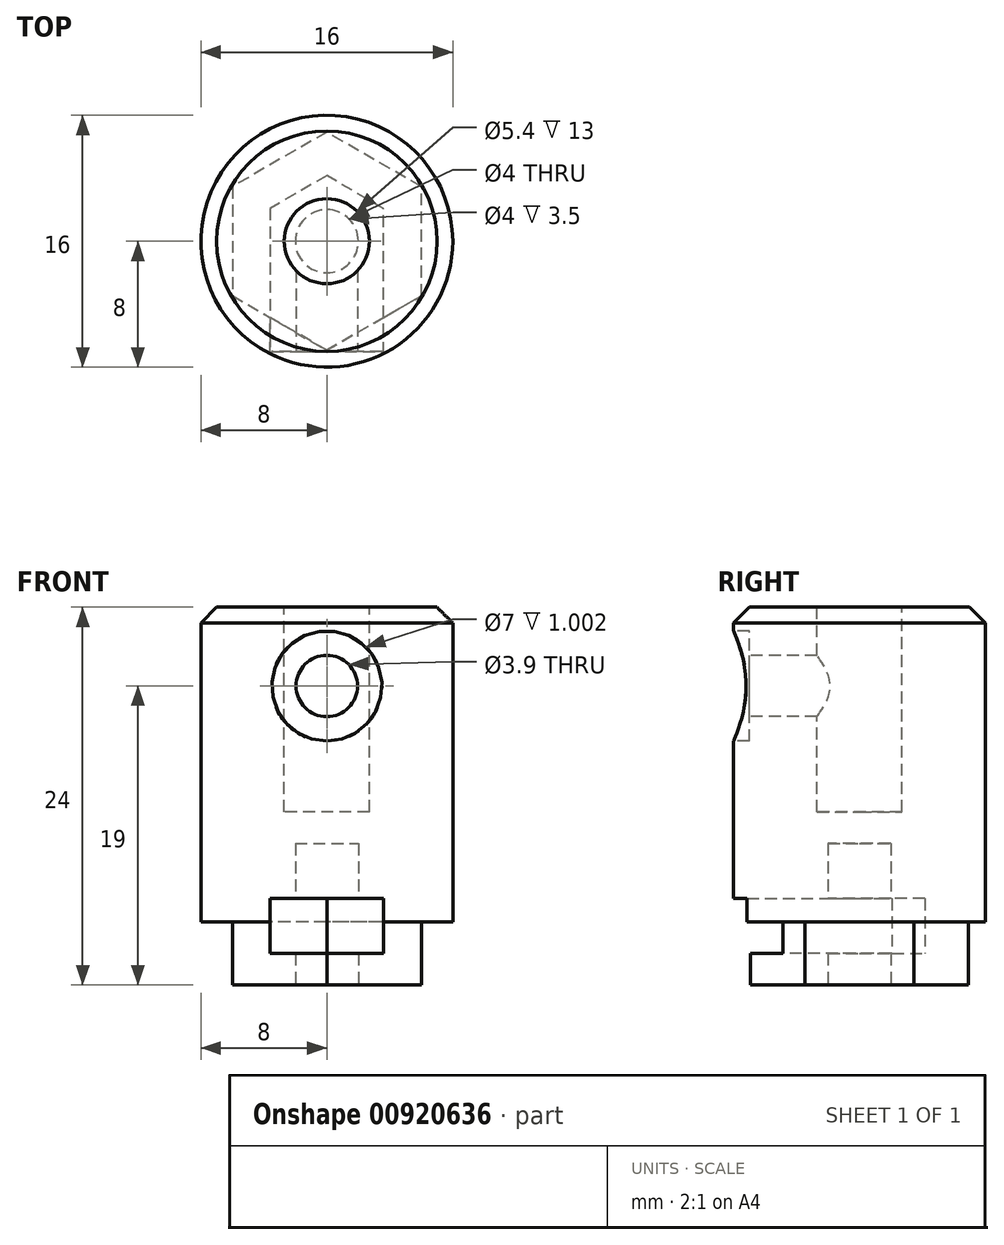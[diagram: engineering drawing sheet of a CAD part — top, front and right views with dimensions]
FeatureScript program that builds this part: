
annotation { "Feature Type Name" : "Feature", "Feature Type Description" : "" }
export const myFeature = defineFeature(function(context is Context, id is Id, definition is map)
    precondition{}
    {
        {
            assignVariable(context, id + "F0", {"name" : "len", "anyValue" : 20 * mm});
        }
        {
            var Q0;
            Q0=qCreatedBy(makeId("Top.planeOp"),FACE);
            var sketch = newSketch(context, id + "F1", { "sketchPlane" : qUnion([Q0])});
            skCircle(sketch, "E0", {"center": v(0, 0) * mm, "radius": 8 * mm});
            skSolve(sketch);
        }
        {
            var Q0;
            Q0=makeQuery(id+"F1.imprint","IMPRINT",FACE,{"disambiguationData":[TD([[makeQuery(id+"F1.imprint","IMPRINT",EDGE,{"derivedFrom":sQuery(id+"F1.wireOp",EDGE,"E0")}),1.0]])]});
            var Q1;
            Q1=sQuery(id+"F1.wireOp",EDGE,"E0");
            extrude(context, id + "F2", {"entities" : qUnion([Q0]), "surfaceEntities" : qUnion([Q1]), "depth" : getVariable(context, 'len'), "offsetDistance" : 25 * mm});
        }
        {
            var Q0;
            Q0=makeQuery(id+"F2.opExtrude","CAP_FACE",FACE,{"disambiguationData":[OSD([sQuery(id+"F1.wireOp",EDGE,"E0")])],"isStart":true});
            var sketch = newSketch(context, id + "F3", { "sketchPlane" : qUnion([Q0])});
            skCircle(sketch, "E1.cCircle", {"center": v(0, 0) * mm, "radius": 6 * mm, "construction": true});
            skLineSegment(sketch, "E1.0", {"start": v(-6, -3.46) * mm, "end": v(-6, 3.46) * mm});
            skLineSegment(sketch, "E1.1", {"start": v(-6, 3.46) * mm, "end": v(0, 6.93) * mm});
            skLineSegment(sketch, "E1.2", {"start": v(0, 6.93) * mm, "end": v(6, 3.46) * mm});
            skLineSegment(sketch, "E1.3", {"start": v(6, 3.46) * mm, "end": v(6, -3.46) * mm});
            skLineSegment(sketch, "E1.4", {"start": v(6, -3.46) * mm, "end": v(0, -6.93) * mm});
            skLineSegment(sketch, "E1.5", {"start": v(0, -6.93) * mm, "end": v(-6, -3.46) * mm});
            skPoint(sketch, "E1.0.midPoint", {"position": v(-6, 0) * mm});
            skSolve(sketch);
        }
        {
            var Q0;
            Q0 = qSketchRegion(id + "F3", true);
            extrude(context, id + "F4", {"entities" : qUnion([Q0]), "operationType" : NewBodyOperationType.ADD, "depth" : 4 * mm, "offsetDistance" : 25 * mm});
        }
        {
            var Q0;
            Q0=makeQuery(id+"F4.opExtrude","CAP_FACE",FACE,{"disambiguationData":[OSD([sQuery(id+"F3.wireOp",EDGE,"E1.0"),sQuery(id+"F3.wireOp",EDGE,"E1.1"),sQuery(id+"F3.wireOp",EDGE,"E1.2"),sQuery(id+"F3.wireOp",EDGE,"E1.3"),sQuery(id+"F3.wireOp",EDGE,"E1.4"),sQuery(id+"F3.wireOp",EDGE,"E1.5")])],"isStart":false});
            var sketch = newSketch(context, id + "F5", { "sketchPlane" : qUnion([Q0])});
            skCircle(sketch, "E2", {"center": v(0, 0) * mm, "radius": 2 * mm});
            skSolve(sketch);
        }
        {
            var Q0;
            Q0 = qSketchRegion(id + "F5", true);
            extrude(context, id + "F6", {"entities" : qUnion([Q0]), "operationType" : NewBodyOperationType.REMOVE, "oppositeDirection" : true, "depth" : 9 * mm, "offsetDistance" : 25 * mm});
        }
        {
            var Q0;
            Q0=makeQuery(id+"F4.opExtrude","CAP_FACE",FACE,{"disambiguationData":[OSD([sQuery(id+"F3.wireOp",EDGE,"E1.0"),sQuery(id+"F3.wireOp",EDGE,"E1.1"),sQuery(id+"F3.wireOp",EDGE,"E1.2"),sQuery(id+"F3.wireOp",EDGE,"E1.3"),sQuery(id+"F3.wireOp",EDGE,"E1.4"),sQuery(id+"F3.wireOp",EDGE,"E1.5")])],"isStart":false});
            cPlane(context, id + "F7", {"entities" : qUnion([Q0]), "cplaneType" : CPlaneType.OFFSET, "offset" : 2 * mm, "oppositeDirection" : true, "width" : 150 * mm, "height" : 150 * mm});
        }
        {
            var Q0;
            Q0=qCreatedBy(id+"F7.planeOp",FACE);
            var sketch = newSketch(context, id + "F8", { "sketchPlane" : qUnion([Q0])});
            skCircle(sketch, "E3.cCircle", {"center": v(0, 0) * mm, "radius": 3.6 * mm, "construction": true});
            skLineSegment(sketch, "E3.0", {"start": v(3.6, 2.08) * mm, "end": v(3.6, -2.08) * mm});
            skLineSegment(sketch, "E3.1", {"start": v(3.6, -2.08) * mm, "end": v(0, -4.16) * mm});
            skLineSegment(sketch, "E3.2", {"start": v(0, -4.16) * mm, "end": v(-3.6, -2.08) * mm});
            skLineSegment(sketch, "E3.3", {"start": v(-3.6, -2.08) * mm, "end": v(-3.6, 2.08) * mm});
            skLineSegment(sketch, "E3.4", {"start": v(-3.6, 2.08) * mm, "end": v(0, 4.16) * mm});
            skLineSegment(sketch, "E3.5", {"start": v(0, 4.16) * mm, "end": v(3.6, 2.08) * mm});
            skPoint(sketch, "E3.0.midPoint", {"position": v(3.6, 0) * mm});
            skSolve(sketch);
        }
        {
            var Q0;
            Q0 = qSketchRegion(id + "F8", true);
            extrude(context, id + "F9", {"entities" : qUnion([Q0]), "operationType" : NewBodyOperationType.REMOVE, "oppositeDirection" : true, "depth" : 3.5 * mm, "offsetDistance" : 25 * mm});
        }
        {
            var Q0;
            Q0=qCreatedBy(makeId("Front.planeOp"),FACE);
            var sketch = newSketch(context, id + "F10", { "sketchPlane" : qUnion([Q0])});
            skLineSegment(sketch, "E4.bottom", {"start": v(-3.6, 1.5) * mm, "end": v(3.6, 1.5) * mm});
            skLineSegment(sketch, "E4.top", {"start": v(-3.6, -2) * mm, "end": v(3.6, -2) * mm});
            skLineSegment(sketch, "E4.left", {"start": v(-3.6, 1.5) * mm, "end": v(-3.6, -2) * mm});
            skLineSegment(sketch, "E4.right", {"start": v(3.6, 1.5) * mm, "end": v(3.6, -2) * mm});
            skSolve(sketch);
        }
        {
            var Q0;
            Q0 = qSketchRegion(id + "F10", true);
            extrude(context, id + "F11", {"entities" : qUnion([Q0]), "operationType" : NewBodyOperationType.REMOVE, "depth" : 9 * mm, "offsetDistance" : 25 * mm});
        }
        {
            var Q0;
            Q0=makeQuery(id+"F2.opExtrude","CAP_EDGE",EDGE,{"disambiguationData":[OSD([sQuery(id+"F1.wireOp",EDGE,"E0")])],"isStart":false});
            chamfer(context, id + "F12", {"entities" : qUnion([Q0]), "width" : 1 * mm, "tangentPropagation" : true});
        }
        {
            var Q0;
            Q0=makeQuery(id+"F2.opExtrude","CAP_FACE",FACE,{"disambiguationData":[OSD([sQuery(id+"F1.wireOp",EDGE,"E0")])],"isStart":false});
            var sketch = newSketch(context, id + "F13", { "sketchPlane" : qUnion([Q0])});
            skCircle(sketch, "E5", {"center": v(0, 0) * mm, "radius": 2.7 * mm});
            skSolve(sketch);
        }
        {
            var Q0;
            Q0 = qSketchRegion(id + "F13", true);
            extrude(context, id + "F14", {"entities" : qUnion([Q0]), "operationType" : NewBodyOperationType.REMOVE, "oppositeDirection" : true, "depth" : 13 * mm, "offsetDistance" : 25 * mm});
        }
        {
            var Q0;
            Q0=qCreatedBy(makeId("Front.planeOp"),FACE);
            cPlane(context, id + "F15", {"entities" : qUnion([Q0]), "cplaneType" : CPlaneType.OFFSET, "offset" : 8 * mm, "width" : 150 * mm, "height" : 150 * mm});
        }
        {
            var Q0;
            Q0=qCreatedBy(id+"F15.planeOp",FACE);
            var sketch = newSketch(context, id + "F16", { "sketchPlane" : qUnion([Q0])});
            skPoint(sketch, "E6", {"position": v(0, 15) * mm});
            skSolve(sketch);
        }
        {
            var Q0;
            Q0=sQuery(id+"F16.wireOp",VERTEX,"E6");
            var Q1;
            Q1=makeQuery(id+"F2.opExtrude","SWEPT_BODY",BODY,{"disambiguationData":[OSD([sQuery(id+"F1.wireOp",EDGE,"E0")])]});
            hole(context, id + "F17", {"style" : HoleStyle.C_BORE, "endStyle" : HoleEndStyle.BLIND, "holeDiameter" : 3.9 * mm, "cBoreDiameter" : 7 * mm, "cBoreDepth" : 1 * mm, "majorDiameter" : 5 * mm, "holeDepth" : 9 * mm, "isTappedThrough" : true, "tappedDepth" : 12 * mm, "tapClearance" : 3, "startFromSketch" : true, "locations" : qUnion([Q0]), "scope" : qUnion([Q1])});
        }
    });
